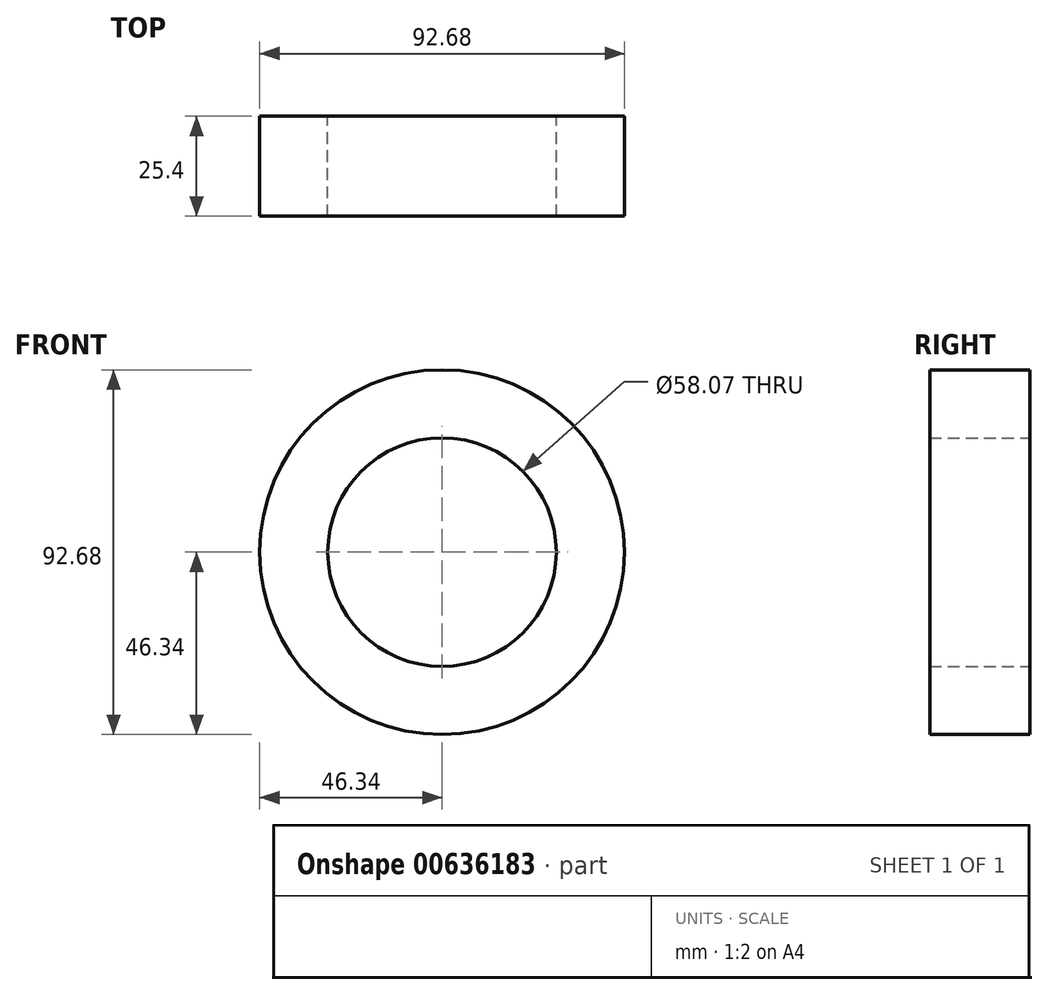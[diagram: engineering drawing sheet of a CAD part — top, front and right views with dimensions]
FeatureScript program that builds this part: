
annotation { "Feature Type Name" : "Feature", "Feature Type Description" : "" }
export const myFeature = defineFeature(function(context is Context, id is Id, definition is map)
    precondition{}
    {
        {
            var Q0;
            Q0=qCreatedBy(makeId("Front.planeOp"),FACE);
            var sketch = newSketch(context, id + "F0", { "sketchPlane" : qUnion([Q0])});
            skCircle(sketch, "E0", {"center": v(0, 0) * mm, "radius": 29.03 * mm});
            skCircle(sketch, "E1", {"center": v(0, 0) * mm, "radius": 46.34 * mm});
            skSolve(sketch);
        }
        {
            var Q0;
            Q0=makeQuery(id+"F0.imprint","IMPRINT",FACE,{"disambiguationData":[TD([[makeQuery(id+"F0.imprint","IMPRINT",EDGE,{"derivedFrom":sQuery(id+"F0.wireOp",EDGE,"E0")}),-1.0]])]});
            extrude(context, id + "F1", {"entities" : qUnion([Q0]), "depth" : 25.4 * mm, "offsetDistance" : 25.4 * mm});
        }
    });
